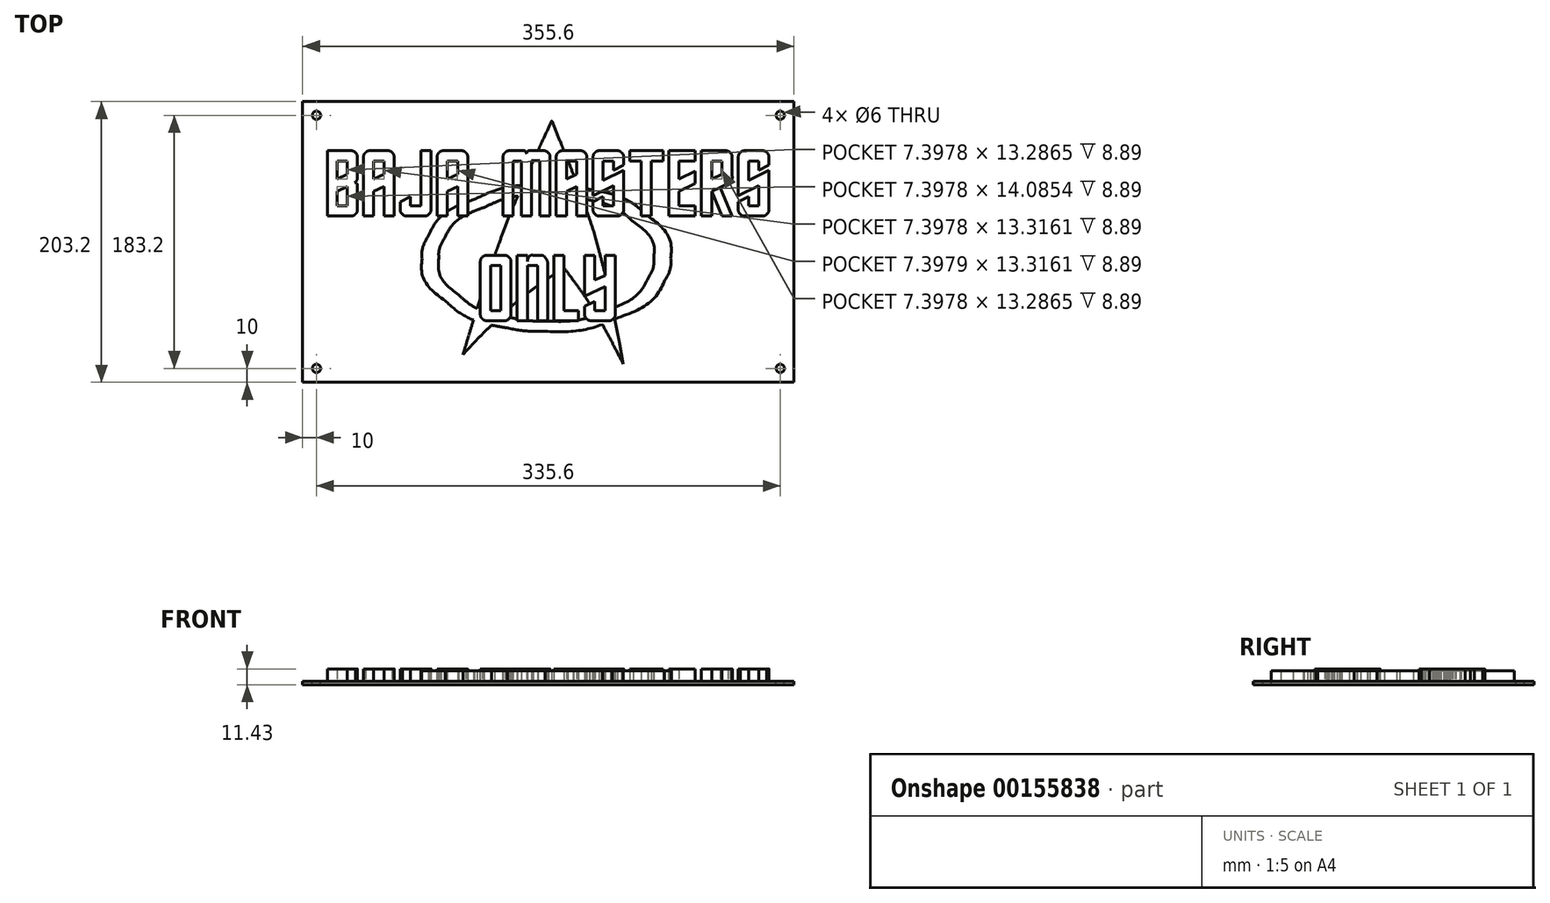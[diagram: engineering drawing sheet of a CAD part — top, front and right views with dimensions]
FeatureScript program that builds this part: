
annotation { "Feature Type Name" : "Feature", "Feature Type Description" : "" }
export const myFeature = defineFeature(function(context is Context, id is Id, definition is map)
    precondition{}
    {
        {
            var Q0;
            Q0=qCreatedBy(makeId("Top.planeOp"),FACE);
            var sketch = newSketch(context, id + "F0", { "sketchPlane" : qUnion([Q0])});
            skLineSegment(sketch, "E0.bottom", {"start": v(177.8, -101.6) * mm, "end": v(-177.8, -101.6) * mm});
            skLineSegment(sketch, "E0.top", {"start": v(177.8, 101.6) * mm, "end": v(-177.8, 101.6) * mm});
            skLineSegment(sketch, "E0.left", {"start": v(177.8, -101.6) * mm, "end": v(177.8, 101.6) * mm});
            skLineSegment(sketch, "E0.right", {"start": v(-177.8, -101.6) * mm, "end": v(-177.8, 101.6) * mm});
            skPoint(sketch, "E0.middle", {"position": v(0, 0) * mm});
            skCircle(sketch, "E1", {"center": v(-167.8, 91.6) * mm, "radius": 3 * mm});
            skCircle(sketch, "E2", {"center": v(-167.8, -91.6) * mm, "radius": 3 * mm});
            skCircle(sketch, "E3", {"center": v(167.8, 91.6) * mm, "radius": 3 * mm});
            skCircle(sketch, "E4", {"center": v(167.8, -91.6) * mm, "radius": 3 * mm});
            skSolve(sketch);
        }
        {
            var Q0;
            Q0=makeQuery(id+"F0.imprint","IMPRINT",FACE,{"disambiguationData":[TD([[makeQuery(id+"F0.imprint","IMPRINT",EDGE,{"derivedFrom":sQuery(id+"F0.wireOp",EDGE,"E0.bottom")}),-1.0]])]});
            var sketch = newSketch(context, id + "F1", { "sketchPlane" : qUnion([Q0])});
            skFitSpline(sketch, "E5", {"points": [v(54.28, -88.47) * mm, v(50.86, -81.9) * mm, v(48.15, -76.64) * mm, v(46.12, -72.72) * mm]});
            skFitSpline(sketch, "E6", {"points": [v(46.12, -72.72) * mm, v(39.8, -60.96) * mm, v(34.36, -51.6) * mm, v(29.8, -44.65) * mm]});
            skFitSpline(sketch, "E7", {"points": [v(29.8, -44.65) * mm, v(26.65, -39.85) * mm, v(22.73, -34.22) * mm, v(18.05, -27.77) * mm]});
            skFitSpline(sketch, "E8", {"points": [v(18.05, -27.77) * mm, v(16.4, -25.5) * mm, v(14.13, -22.46) * mm, v(11.22, -18.67) * mm]});
            skFitSpline(sketch, "E9", {"points": [v(11.22, -18.67) * mm, v(6.54, -21.83) * mm, v(2.88, -24.36) * mm, v(0.22, -26.25) * mm]});
            skFitSpline(sketch, "E10", {"points": [v(0.22, -26.25) * mm, v(-8.5, -32.32) * mm, v(-15.02, -37.13) * mm, v(-19.32, -40.67) * mm]});
            skFitSpline(sketch, "E11", {"points": [v(-19.32, -40.67) * mm, v(-25.13, -45.35) * mm, v(-31.45, -50.97) * mm, v(-38.28, -57.55) * mm]});
            skFitSpline(sketch, "E12", {"points": [v(-38.28, -57.55) * mm, v(-44.23, -63.24) * mm, v(-49.73, -68.74) * mm, v(-54.78, -74.05) * mm]});
            skFitSpline(sketch, "E13", {"points": [v(-54.78, -74.05) * mm, v(-57.19, -76.58) * mm, v(-59.53, -79.1) * mm, v(-61.8, -81.64) * mm]});
            skFitSpline(sketch, "E14", {"points": [v(-61.8, -81.64) * mm, v(-60.41, -77.09) * mm, v(-59.02, -72.47) * mm, v(-57.63, -67.8) * mm]});
            skFitSpline(sketch, "E15", {"points": [v(-57.63, -67.8) * mm, v(-53.08, -53) * mm, v(-49.73, -42.31) * mm, v(-47.58, -35.74) * mm]});
            skFitSpline(sketch, "E16", {"points": [v(-47.58, -35.74) * mm, v(-43.53, -23.47) * mm, v(-39.48, -11.71) * mm, v(-35.44, -0.46) * mm]});
            skFitSpline(sketch, "E17", {"points": [v(-35.44, -0.46) * mm, v(-31.26, 10.92) * mm, v(-26.08, 23.76) * mm, v(-19.88, 38.05) * mm]});
            skFitSpline(sketch, "E18", {"points": [v(-19.88, 38.05) * mm, v(-14.83, 49.8) * mm, v(-9.7, 61.31) * mm, v(-4.52, 72.57) * mm]});
            skFitSpline(sketch, "E19", {"points": [v(-4.52, 72.57) * mm, v(0.03, 82.43) * mm, v(2.37, 87.36) * mm, v(2.5, 87.36) * mm]});
            skFitSpline(sketch, "E20", {"points": [v(2.5, 87.36) * mm, v(2.62, 87.36) * mm, v(4.77, 82.18) * mm, v(8.95, 71.8) * mm]});
            skFitSpline(sketch, "E21", {"points": [v(8.95, 71.8) * mm, v(13.88, 59.67) * mm, v(18.56, 47.53) * mm, v(22.98, 35.39) * mm]});
            skFitSpline(sketch, "E22", {"points": [v(22.98, 35.39) * mm, v(29.05, 18.7) * mm, v(33.6, 4.73) * mm, v(36.64, -6.53) * mm]});
            skFitSpline(sketch, "E23", {"points": [v(36.64, -6.53) * mm, v(39.17, -15.76) * mm, v(41.95, -27.46) * mm, v(44.98, -41.62) * mm]});
            skFitSpline(sketch, "E24", {"points": [v(44.98, -41.62) * mm, v(47.51, -53.25) * mm, v(49.73, -64.06) * mm, v(51.62, -74.05) * mm]});
            skFitSpline(sketch, "E25", {"points": [v(51.62, -74.05) * mm, v(52.5, -78.86) * mm, v(53.4, -83.66) * mm, v(54.28, -88.47) * mm]});
            skFitSpline(sketch, "E26", {"points": [v(84.06, -28.34) * mm, v(77.86, -39.34) * mm, v(66.67, -48.2) * mm, v(50.48, -54.9) * mm]});
            skFitSpline(sketch, "E27", {"points": [v(50.48, -54.9) * mm, v(34.43, -61.47) * mm, v(16.79, -64.76) * mm, v(-2.43, -64.76) * mm]});
            skFitSpline(sketch, "E28", {"points": [v(-2.43, -64.76) * mm, v(-11.92, -64.76) * mm, v(-21.02, -63.94) * mm, v(-29.75, -62.3) * mm]});
            skFitSpline(sketch, "E29", {"points": [v(-29.75, -62.3) * mm, v(-48.34, -58.5) * mm, v(-63.26, -51.99) * mm, v(-74.51, -42.76) * mm]});
            skFitSpline(sketch, "E30", {"points": [v(-74.51, -42.76) * mm, v(-85.76, -33.4) * mm, v(-91.4, -23.16) * mm, v(-91.4, -12.03) * mm]});
            skFitSpline(sketch, "E31", {"points": [v(-91.4, -12.03) * mm, v(-91.4, -6.46) * mm, v(-89.81, -0.96) * mm, v(-86.65, 4.47) * mm]});
            skFitSpline(sketch, "E32", {"points": [v(-86.65, 4.47) * mm, v(-80.45, 15.47) * mm, v(-69.39, 24.26) * mm, v(-53.46, 30.84) * mm]});
            skFitSpline(sketch, "E33", {"points": [v(-53.46, 30.84) * mm, v(-37.52, 37.54) * mm, v(-19.95, 40.9) * mm, v(-0.73, 40.9) * mm]});
            skFitSpline(sketch, "E34", {"points": [v(-0.73, 40.9) * mm, v(9, 40.9) * mm, v(18.24, 40.07) * mm, v(26.96, 38.42) * mm]});
            skFitSpline(sketch, "E35", {"points": [v(26.96, 38.42) * mm, v(45.55, 34.76) * mm, v(60.47, 28.25) * mm, v(71.73, 18.89) * mm]});
            skFitSpline(sketch, "E36", {"points": [v(71.73, 18.89) * mm, v(82.98, 9.53) * mm, v(88.6, -0.77) * mm, v(88.6, -12.03) * mm]});
            skFitSpline(sketch, "E37", {"points": [v(88.6, -12.03) * mm, v(88.6, -17.34) * mm, v(87.1, -22.78) * mm, v(84.06, -28.34) * mm]});
            skFitSpline(sketch, "E38", {"points": [v(72.1, -26.25) * mm, v(74.89, -21.58) * mm, v(76.28, -16.77) * mm, v(76.28, -11.84) * mm]});
            skFitSpline(sketch, "E39", {"points": [v(76.28, -11.84) * mm, v(76.28, -2.23) * mm, v(71.35, 6.56) * mm, v(61.49, 14.53) * mm]});
            skFitSpline(sketch, "E40", {"points": [v(61.49, 14.53) * mm, v(51.75, 22.62) * mm, v(38.85, 28.25) * mm, v(22.8, 31.4) * mm]});
            skFitSpline(sketch, "E41", {"points": [v(22.8, 31.4) * mm, v(14.83, 32.92) * mm, v(6.8, 33.68) * mm, v(-1.3, 33.68) * mm]});
            skFitSpline(sketch, "E42", {"points": [v(-1.3, 33.68) * mm, v(-17.6, 33.68) * mm, v(-32.66, 30.77) * mm, v(-46.44, 24.96) * mm]});
            skFitSpline(sketch, "E43", {"points": [v(-46.44, 24.96) * mm, v(-60.22, 19.27) * mm, v(-69.83, 11.74) * mm, v(-75.27, 2.39) * mm]});
            skFitSpline(sketch, "E44", {"points": [v(-75.27, 2.39) * mm, v(-77.92, -2.42) * mm, v(-79.25, -7.16) * mm, v(-79.25, -11.84) * mm]});
            skFitSpline(sketch, "E45", {"points": [v(-79.25, -11.84) * mm, v(-79.25, -21.45) * mm, v(-74.45, -30.3) * mm, v(-64.84, -38.4) * mm]});
            skFitSpline(sketch, "E46", {"points": [v(-64.84, -38.4) * mm, v(-55.1, -46.36) * mm, v(-42.14, -51.92) * mm, v(-25.95, -55.08) * mm]});
            skFitSpline(sketch, "E47", {"points": [v(-25.95, -55.08) * mm, v(-17.73, -56.6) * mm, v(-9.58, -57.36) * mm, v(-1.49, -57.36) * mm]});
            skFitSpline(sketch, "E48", {"points": [v(-1.49, -57.36) * mm, v(14.95, -57.36) * mm, v(29.94, -54.58) * mm, v(43.47, -49.02) * mm]});
            skFitSpline(sketch, "E49", {"points": [v(43.47, -49.02) * mm, v(57.12, -43.32) * mm, v(66.67, -35.74) * mm, v(72.1, -26.25) * mm]});
            skSolve(sketch);
        }
        {
            var Q0;
            Q0 = qSketchRegion(id + "F1", true);
            var Q1;
            {var subQ8=sQuery(id+"F1.wireOp",EDGE,"E7");Q1=makeQuery(id+"F1.imprint","IMPRINT",FACE,{"disambiguationData":[TD([[makeQuery(id+"F1.imprint","IMPRINT",EDGE,{"derivedFrom":subQ8}),-1.0]])]});}
            extrude(context, id + "F2", {"entities" : qUnion([Q0, Q1]), "depth" : 7.62 * mm});
        }
        {
            var Q0;
            Q0=makeQuery(id+"F0.imprint","IMPRINT",FACE,{"disambiguationData":[TD([[makeQuery(id+"F0.imprint","IMPRINT",EDGE,{"derivedFrom":sQuery(id+"F0.wireOp",EDGE,"E0.bottom")}),-1.0]])]});
            extrude(context, id + "F3", {"entities" : qUnion([Q0]), "operationType" : NewBodyOperationType.ADD, "oppositeDirection" : true, "depth" : 2.54 * mm});
        }
        {
            var Q0;
            Q0=qCreatedBy(makeId("Top.planeOp"),FACE);
            var sketch = newSketch(context, id + "F4", { "sketchPlane" : qUnion([Q0])});
            skLineSegment(sketch, "E50", {"start": v(-145.58, 58.6) * mm, "end": v(-152.98, 58.6) * mm});
            skLineSegment(sketch, "E51", {"start": v(-152.98, 58.6) * mm, "end": v(-152.98, 45.32) * mm});
            skLineSegment(sketch, "E52", {"start": v(-152.98, 45.32) * mm, "end": v(-145.58, 49) * mm});
            skLineSegment(sketch, "E53", {"start": v(-145.58, 49) * mm, "end": v(-145.58, 58.6) * mm});
            skLineSegment(sketch, "E54", {"start": v(-145.58, 40.14) * mm, "end": v(-152.98, 36.45) * mm});
            skLineSegment(sketch, "E55", {"start": v(-152.98, 36.45) * mm, "end": v(-152.98, 26.06) * mm});
            skLineSegment(sketch, "E56", {"start": v(-152.98, 26.06) * mm, "end": v(-145.58, 26.06) * mm});
            skLineSegment(sketch, "E57", {"start": v(-145.58, 26.06) * mm, "end": v(-145.58, 40.14) * mm});
            skFitSpline(sketch, "E58", {"points": [v(-138.19, 26.06) * mm, v(-138.19, 23.1) * mm, v(-138.68, 21.13) * mm, v(-139.67, 20.14) * mm]});
            skFitSpline(sketch, "E59", {"points": [v(-139.67, 20.14) * mm, v(-140.65, 19.15) * mm, v(-142.62, 18.66) * mm, v(-145.58, 18.66) * mm]});
            skLineSegment(sketch, "E60", {"start": v(-138.19, 39.37) * mm, "end": v(-138.19, 26.06) * mm});
            skLineSegment(sketch, "E61", {"start": v(-138.19, 26.06) * mm, "end": v(-138.19, 39.37) * mm});
            skFitSpline(sketch, "E62", {"points": [v(-145.58, 66) * mm, v(-142.62, 66) * mm, v(-140.65, 65.51) * mm, v(-139.67, 64.53) * mm]});
            skFitSpline(sketch, "E63", {"points": [v(-139.67, 64.53) * mm, v(-138.68, 63.54) * mm, v(-138.19, 61.57) * mm, v(-138.19, 58.6) * mm]});
            skLineSegment(sketch, "E64", {"start": v(-145.58, 18.66) * mm, "end": v(-160.38, 18.66) * mm});
            skLineSegment(sketch, "E65", {"start": v(-159.7, 18.66) * mm, "end": v(-159.7, 66) * mm});
            skLineSegment(sketch, "E66", {"start": v(-160.38, 66) * mm, "end": v(-145.58, 66) * mm});
            skLineSegment(sketch, "E67", {"start": v(-145.58, 66) * mm, "end": v(-145.58, 18.66) * mm});
            skFitSpline(sketch, "E68", {"points": [v(-138.19, 48.25) * mm, v(-138.19, 45.79) * mm, v(-138.88, 44.01) * mm, v(-140.26, 42.93) * mm]});
            skFitSpline(sketch, "E69", {"points": [v(-140.26, 42.93) * mm, v(-138.9, 42.51) * mm, v(-138.2, 41.33) * mm, v(-138.19, 39.37) * mm]});
            skLineSegment(sketch, "E70", {"start": v(-138.19, 58.6) * mm, "end": v(-138.19, 48.25) * mm});
            skLineSegment(sketch, "E71", {"start": v(-138.19, 48.25) * mm, "end": v(-138.19, 58.6) * mm});
            skFitSpline(sketch, "E72", {"points": [v(-133.75, 58.6) * mm, v(-133.75, 61.57) * mm, v(-133.25, 63.54) * mm, v(-132.27, 64.53) * mm]});
            skFitSpline(sketch, "E73", {"points": [v(-132.27, 64.53) * mm, v(-131.28, 65.51) * mm, v(-129.3, 66) * mm, v(-126.35, 66) * mm]});
            skLineSegment(sketch, "E74", {"start": v(-126.35, 58.6) * mm, "end": v(-126.35, 45.3) * mm});
            skLineSegment(sketch, "E75", {"start": v(-126.35, 45.3) * mm, "end": v(-118.95, 49) * mm});
            skLineSegment(sketch, "E76", {"start": v(-118.95, 49) * mm, "end": v(-118.95, 58.6) * mm});
            skLineSegment(sketch, "E77", {"start": v(-118.95, 58.6) * mm, "end": v(-126.35, 58.6) * mm});
            skFitSpline(sketch, "E78", {"points": [v(-118.95, 66) * mm, v(-116, 66) * mm, v(-114.02, 65.51) * mm, v(-113.03, 64.53) * mm]});
            skFitSpline(sketch, "E79", {"points": [v(-113.03, 64.53) * mm, v(-112.05, 63.54) * mm, v(-111.55, 61.57) * mm, v(-111.55, 58.6) * mm]});
            skLineSegment(sketch, "E80", {"start": v(-126.35, 66) * mm, "end": v(-118.95, 66) * mm});
            skLineSegment(sketch, "E81", {"start": v(-118.95, 66) * mm, "end": v(-126.35, 66) * mm});
            skLineSegment(sketch, "E82", {"start": v(-111.55, 58.6) * mm, "end": v(-111.55, 18.66) * mm});
            skLineSegment(sketch, "E83", {"start": v(-111.55, 18.66) * mm, "end": v(-118.95, 18.66) * mm});
            skLineSegment(sketch, "E84", {"start": v(-118.95, 18.66) * mm, "end": v(-118.95, 40.11) * mm});
            skLineSegment(sketch, "E85", {"start": v(-118.95, 40.11) * mm, "end": v(-126.35, 36.42) * mm});
            skLineSegment(sketch, "E86", {"start": v(-126.35, 36.42) * mm, "end": v(-126.35, 18.66) * mm});
            skLineSegment(sketch, "E87", {"start": v(-126.35, 18.66) * mm, "end": v(-133.75, 18.66) * mm});
            skLineSegment(sketch, "E88", {"start": v(-133.75, 18.66) * mm, "end": v(-133.75, 58.6) * mm});
            skLineSegment(sketch, "E89", {"start": v(-133.75, 58.6) * mm, "end": v(-111.55, 58.6) * mm});
            skFitSpline(sketch, "E90", {"points": [v(-84.92, 26.09) * mm, v(-84.92, 23.15) * mm, v(-85.42, 21.18) * mm, v(-86.43, 20.17) * mm]});
            skFitSpline(sketch, "E91", {"points": [v(-86.43, 20.17) * mm, v(-87.42, 19.18) * mm, v(-89.38, 18.68) * mm, v(-92.32, 18.66) * mm]});
            skLineSegment(sketch, "E92", {"start": v(-84.92, 66) * mm, "end": v(-84.92, 26.09) * mm});
            skLineSegment(sketch, "E93", {"start": v(-84.92, 26.09) * mm, "end": v(-84.92, 66) * mm});
            skFitSpline(sketch, "E94", {"points": [v(-99.72, 18.7) * mm, v(-102.66, 18.7) * mm, v(-104.63, 19.17) * mm, v(-105.64, 20.14) * mm]});
            skFitSpline(sketch, "E95", {"points": [v(-105.64, 20.14) * mm, v(-106.62, 21.1) * mm, v(-107.12, 23.1) * mm, v(-107.12, 26.12) * mm]});
            skLineSegment(sketch, "E96", {"start": v(-92.32, 18.66) * mm, "end": v(-99.72, 18.7) * mm});
            skLineSegment(sketch, "E97", {"start": v(-99.72, 18.7) * mm, "end": v(-92.32, 18.66) * mm});
            skLineSegment(sketch, "E98", {"start": v(-107.12, 26.12) * mm, "end": v(-107.12, 29.05) * mm});
            skLineSegment(sketch, "E99", {"start": v(-107.12, 29.05) * mm, "end": v(-99.72, 32.75) * mm});
            skLineSegment(sketch, "E100", {"start": v(-99.72, 32.75) * mm, "end": v(-99.72, 26.09) * mm});
            skLineSegment(sketch, "E101", {"start": v(-99.72, 26.09) * mm, "end": v(-92.32, 26.09) * mm});
            skLineSegment(sketch, "E102", {"start": v(-92.32, 26.09) * mm, "end": v(-92.32, 66) * mm});
            skLineSegment(sketch, "E103", {"start": v(-92.32, 66) * mm, "end": v(-84.92, 66) * mm});
            skLineSegment(sketch, "E104", {"start": v(-84.92, 66) * mm, "end": v(-84.92, 66) * mm});
            skFitSpline(sketch, "E105", {"points": [v(-80.48, 58.6) * mm, v(-80.48, 61.57) * mm, v(-79.99, 63.54) * mm, v(-79, 64.53) * mm]});
            skFitSpline(sketch, "E106", {"points": [v(-79, 64.53) * mm, v(-78.02, 65.51) * mm, v(-76.04, 66) * mm, v(-73.09, 66) * mm]});
            skLineSegment(sketch, "E107", {"start": v(-73.09, 58.6) * mm, "end": v(-73.09, 45.3) * mm});
            skLineSegment(sketch, "E108", {"start": v(-73.09, 45.3) * mm, "end": v(-65.69, 49) * mm});
            skLineSegment(sketch, "E109", {"start": v(-65.69, 49) * mm, "end": v(-65.69, 58.6) * mm});
            skLineSegment(sketch, "E110", {"start": v(-65.69, 58.6) * mm, "end": v(-73.09, 58.6) * mm});
            skFitSpline(sketch, "E111", {"points": [v(-65.69, 66) * mm, v(-62.73, 66) * mm, v(-60.76, 65.51) * mm, v(-59.77, 64.53) * mm]});
            skFitSpline(sketch, "E112", {"points": [v(-59.77, 64.53) * mm, v(-58.78, 63.54) * mm, v(-58.29, 61.57) * mm, v(-58.29, 58.6) * mm]});
            skLineSegment(sketch, "E113", {"start": v(-73.09, 66) * mm, "end": v(-65.69, 66) * mm});
            skLineSegment(sketch, "E114", {"start": v(-65.69, 66) * mm, "end": v(-73.09, 66) * mm});
            skFitSpline(sketch, "E115", {"points": [v(-15.77, 63.79) * mm, v(-15.27, 65.27) * mm, v(-14.04, 66) * mm, v(-12.07, 66) * mm]});
            skLineSegment(sketch, "E116", {"start": v(-58.29, 58.6) * mm, "end": v(-58.29, 18.66) * mm});
            skLineSegment(sketch, "E117", {"start": v(-58.29, 18.66) * mm, "end": v(-65.69, 18.66) * mm});
            skLineSegment(sketch, "E118", {"start": v(-65.69, 18.66) * mm, "end": v(-65.69, 40.11) * mm});
            skLineSegment(sketch, "E119", {"start": v(-65.69, 40.11) * mm, "end": v(-73.09, 36.42) * mm});
            skLineSegment(sketch, "E120", {"start": v(-73.09, 36.42) * mm, "end": v(-73.09, 18.66) * mm});
            skLineSegment(sketch, "E121", {"start": v(-73.09, 18.66) * mm, "end": v(-80.48, 18.66) * mm});
            skLineSegment(sketch, "E122", {"start": v(-80.48, 18.66) * mm, "end": v(-80.48, 58.6) * mm});
            skLineSegment(sketch, "E123", {"start": v(-80.48, 58.6) * mm, "end": v(-58.29, 58.6) * mm});
            skFitSpline(sketch, "E124", {"points": [v(-6.15, 66) * mm, v(-3.2, 66) * mm, v(-1.22, 65.51) * mm, v(-0.23, 64.53) * mm]});
            skFitSpline(sketch, "E125", {"points": [v(-0.23, 64.53) * mm, v(0.75, 63.54) * mm, v(1.25, 61.58) * mm, v(1.25, 58.64) * mm]});
            skLineSegment(sketch, "E126", {"start": v(-12.07, 66) * mm, "end": v(-6.15, 66) * mm});
            skLineSegment(sketch, "E127", {"start": v(-6.15, 66) * mm, "end": v(-12.07, 66) * mm});
            skFitSpline(sketch, "E128", {"points": [v(-32.78, 58.6) * mm, v(-32.78, 61.57) * mm, v(-32.29, 63.54) * mm, v(-31.3, 64.53) * mm]});
            skFitSpline(sketch, "E129", {"points": [v(-31.3, 64.53) * mm, v(-30.32, 65.51) * mm, v(-28.34, 66) * mm, v(-25.38, 66) * mm]});
            skLineSegment(sketch, "E130", {"start": v(1.25, 58.64) * mm, "end": v(1.25, 18.66) * mm});
            skLineSegment(sketch, "E131", {"start": v(1.25, 18.66) * mm, "end": v(-6.15, 18.66) * mm});
            skLineSegment(sketch, "E132", {"start": v(-6.15, 18.66) * mm, "end": v(-6.15, 58.64) * mm});
            skLineSegment(sketch, "E133", {"start": v(-6.15, 58.64) * mm, "end": v(-12.07, 58.64) * mm});
            skLineSegment(sketch, "E134", {"start": v(-12.07, 58.64) * mm, "end": v(-12.07, 18.66) * mm});
            skLineSegment(sketch, "E135", {"start": v(-12.07, 18.66) * mm, "end": v(-19.47, 18.66) * mm});
            skLineSegment(sketch, "E136", {"start": v(-19.47, 18.66) * mm, "end": v(-19.47, 58.64) * mm});
            skLineSegment(sketch, "E137", {"start": v(-19.47, 58.64) * mm, "end": v(-25.38, 58.64) * mm});
            skLineSegment(sketch, "E138", {"start": v(-25.38, 58.64) * mm, "end": v(-25.38, 18.66) * mm});
            skLineSegment(sketch, "E139", {"start": v(-25.38, 18.66) * mm, "end": v(-32.78, 18.66) * mm});
            skLineSegment(sketch, "E140", {"start": v(-32.78, 18.66) * mm, "end": v(-32.78, 58.6) * mm});
            skLineSegment(sketch, "E141", {"start": v(-32.78, 58.6) * mm, "end": v(1.25, 58.64) * mm});
            skFitSpline(sketch, "E142", {"points": [v(-19.47, 66) * mm, v(-17.5, 66) * mm, v(-16.26, 65.27) * mm, v(-15.77, 63.79) * mm]});
            skLineSegment(sketch, "E143", {"start": v(-25.38, 66) * mm, "end": v(-19.47, 66) * mm});
            skLineSegment(sketch, "E144", {"start": v(-19.47, 66) * mm, "end": v(-25.38, 66) * mm});
            skFitSpline(sketch, "E145", {"points": [v(5.69, 58.6) * mm, v(5.69, 61.57) * mm, v(6.18, 63.54) * mm, v(7.17, 64.53) * mm]});
            skFitSpline(sketch, "E146", {"points": [v(7.17, 64.53) * mm, v(8.15, 65.51) * mm, v(10.13, 66) * mm, v(13.08, 66) * mm]});
            skLineSegment(sketch, "E147", {"start": v(13.08, 58.6) * mm, "end": v(13.08, 45.3) * mm});
            skLineSegment(sketch, "E148", {"start": v(13.08, 45.3) * mm, "end": v(20.48, 49) * mm});
            skLineSegment(sketch, "E149", {"start": v(20.48, 49) * mm, "end": v(20.48, 58.6) * mm});
            skLineSegment(sketch, "E150", {"start": v(20.48, 58.6) * mm, "end": v(13.08, 58.6) * mm});
            skFitSpline(sketch, "E151", {"points": [v(20.48, 66) * mm, v(23.44, 66) * mm, v(25.41, 65.51) * mm, v(26.4, 64.53) * mm]});
            skFitSpline(sketch, "E152", {"points": [v(26.4, 64.53) * mm, v(27.39, 63.54) * mm, v(27.88, 61.57) * mm, v(27.88, 58.6) * mm]});
            skLineSegment(sketch, "E153", {"start": v(13.08, 66) * mm, "end": v(20.48, 66) * mm});
            skLineSegment(sketch, "E154", {"start": v(20.48, 66) * mm, "end": v(13.08, 66) * mm});
            skFitSpline(sketch, "E155", {"points": [v(32.32, 58.6) * mm, v(32.32, 61.55) * mm, v(32.81, 63.51) * mm, v(33.8, 64.5) * mm]});
            skFitSpline(sketch, "E156", {"points": [v(33.8, 64.5) * mm, v(34.8, 65.5) * mm, v(36.78, 66.02) * mm, v(39.72, 66.04) * mm]});
            skLineSegment(sketch, "E157", {"start": v(27.88, 58.6) * mm, "end": v(27.88, 18.66) * mm});
            skLineSegment(sketch, "E158", {"start": v(27.88, 18.66) * mm, "end": v(20.48, 18.66) * mm});
            skLineSegment(sketch, "E159", {"start": v(20.48, 18.66) * mm, "end": v(20.48, 40.11) * mm});
            skLineSegment(sketch, "E160", {"start": v(20.48, 40.11) * mm, "end": v(13.08, 36.42) * mm});
            skLineSegment(sketch, "E161", {"start": v(13.08, 36.42) * mm, "end": v(13.08, 18.66) * mm});
            skLineSegment(sketch, "E162", {"start": v(13.08, 18.66) * mm, "end": v(5.69, 18.66) * mm});
            skLineSegment(sketch, "E163", {"start": v(5.69, 18.66) * mm, "end": v(5.69, 58.6) * mm});
            skLineSegment(sketch, "E164", {"start": v(5.69, 58.6) * mm, "end": v(27.88, 58.6) * mm});
            skFitSpline(sketch, "E165", {"points": [v(47.11, 66) * mm, v(50.05, 66) * mm, v(52.02, 65.52) * mm, v(53, 64.56) * mm]});
            skFitSpline(sketch, "E166", {"points": [v(53, 64.56) * mm, v(54, 63.6) * mm, v(54.51, 61.6) * mm, v(54.51, 58.58) * mm]});
            skLineSegment(sketch, "E167", {"start": v(39.72, 66.04) * mm, "end": v(47.11, 66) * mm});
            skLineSegment(sketch, "E168", {"start": v(47.11, 66) * mm, "end": v(39.72, 66.04) * mm});
            skFitSpline(sketch, "E169", {"points": [v(54.51, 26.09) * mm, v(54.51, 23.15) * mm, v(54, 21.18) * mm, v(53, 20.17) * mm]});
            skFitSpline(sketch, "E170", {"points": [v(53, 20.17) * mm, v(52.02, 19.18) * mm, v(50.05, 18.68) * mm, v(47.11, 18.66) * mm]});
            skLineSegment(sketch, "E171", {"start": v(54.51, 58.58) * mm, "end": v(54.51, 55.65) * mm});
            skLineSegment(sketch, "E172", {"start": v(54.51, 55.65) * mm, "end": v(47.11, 51.95) * mm});
            skLineSegment(sketch, "E173", {"start": v(47.11, 51.95) * mm, "end": v(47.11, 58.6) * mm});
            skLineSegment(sketch, "E174", {"start": v(47.11, 58.6) * mm, "end": v(39.72, 58.6) * mm});
            skLineSegment(sketch, "E175", {"start": v(39.72, 58.6) * mm, "end": v(39.72, 44.55) * mm});
            skLineSegment(sketch, "E176", {"start": v(39.72, 44.55) * mm, "end": v(54.51, 51.95) * mm});
            skLineSegment(sketch, "E177", {"start": v(54.51, 51.95) * mm, "end": v(54.51, 26.09) * mm});
            skFitSpline(sketch, "E178", {"points": [v(39.72, 18.7) * mm, v(36.78, 18.7) * mm, v(34.8, 19.17) * mm, v(33.8, 20.14) * mm]});
            skFitSpline(sketch, "E179", {"points": [v(33.8, 20.14) * mm, v(32.81, 21.1) * mm, v(32.32, 23.1) * mm, v(32.32, 26.12) * mm]});
            skLineSegment(sketch, "E180", {"start": v(47.11, 18.66) * mm, "end": v(39.72, 18.7) * mm});
            skLineSegment(sketch, "E181", {"start": v(39.72, 18.7) * mm, "end": v(47.11, 18.66) * mm});
            skLineSegment(sketch, "E182", {"start": v(32.32, 26.12) * mm, "end": v(32.32, 29.05) * mm});
            skLineSegment(sketch, "E183", {"start": v(32.32, 29.05) * mm, "end": v(39.72, 32.75) * mm});
            skLineSegment(sketch, "E184", {"start": v(39.72, 32.75) * mm, "end": v(39.72, 26.09) * mm});
            skLineSegment(sketch, "E185", {"start": v(39.72, 26.09) * mm, "end": v(47.11, 26.09) * mm});
            skLineSegment(sketch, "E186", {"start": v(47.11, 26.09) * mm, "end": v(47.11, 40.82) * mm});
            skLineSegment(sketch, "E187", {"start": v(47.11, 40.82) * mm, "end": v(32.32, 33.46) * mm});
            skLineSegment(sketch, "E188", {"start": v(32.32, 33.46) * mm, "end": v(32.32, 58.6) * mm});
            skLineSegment(sketch, "E189", {"start": v(67.09, 18.66) * mm, "end": v(67.09, 58.6) * mm});
            skLineSegment(sketch, "E190", {"start": v(67.09, 58.6) * mm, "end": v(58.95, 58.58) * mm});
            skLineSegment(sketch, "E191", {"start": v(58.95, 58.58) * mm, "end": v(58.95, 66) * mm});
            skLineSegment(sketch, "E192", {"start": v(58.95, 66) * mm, "end": v(82.92, 66) * mm});
            skLineSegment(sketch, "E193", {"start": v(82.92, 66) * mm, "end": v(82.92, 58.58) * mm});
            skLineSegment(sketch, "E194", {"start": v(82.92, 58.58) * mm, "end": v(74.49, 58.58) * mm});
            skLineSegment(sketch, "E195", {"start": v(74.49, 58.58) * mm, "end": v(74.49, 18.66) * mm});
            skLineSegment(sketch, "E196", {"start": v(74.49, 18.66) * mm, "end": v(67.09, 18.66) * mm});
            skLineSegment(sketch, "E197", {"start": v(67.09, 18.66) * mm, "end": v(67.09, 18.66) * mm});
            skLineSegment(sketch, "E198", {"start": v(87.12, 66) * mm, "end": v(106.36, 66) * mm});
            skLineSegment(sketch, "E199", {"start": v(106.36, 66) * mm, "end": v(106.36, 58.6) * mm});
            skLineSegment(sketch, "E200", {"start": v(106.36, 58.6) * mm, "end": v(94.52, 58.6) * mm});
            skLineSegment(sketch, "E201", {"start": v(94.52, 58.6) * mm, "end": v(94.52, 45.32) * mm});
            skLineSegment(sketch, "E202", {"start": v(94.52, 45.32) * mm, "end": v(106.36, 51.21) * mm});
            skLineSegment(sketch, "E203", {"start": v(106.36, 51.21) * mm, "end": v(106.36, 42.36) * mm});
            skLineSegment(sketch, "E204", {"start": v(106.36, 42.36) * mm, "end": v(94.52, 36.45) * mm});
            skLineSegment(sketch, "E205", {"start": v(94.52, 36.45) * mm, "end": v(94.52, 26.06) * mm});
            skLineSegment(sketch, "E206", {"start": v(94.52, 26.06) * mm, "end": v(106.36, 26.06) * mm});
            skLineSegment(sketch, "E207", {"start": v(106.36, 26.06) * mm, "end": v(106.33, 18.66) * mm});
            skLineSegment(sketch, "E208", {"start": v(106.33, 18.66) * mm, "end": v(87.12, 18.66) * mm});
            skLineSegment(sketch, "E209", {"start": v(87.12, 18.66) * mm, "end": v(87.12, 66) * mm});
            skLineSegment(sketch, "E210", {"start": v(87.12, 66) * mm, "end": v(87.12, 66) * mm});
            skLineSegment(sketch, "E211", {"start": v(125.6, 58.6) * mm, "end": v(118.2, 58.6) * mm});
            skLineSegment(sketch, "E212", {"start": v(118.2, 58.6) * mm, "end": v(118.2, 45.32) * mm});
            skLineSegment(sketch, "E213", {"start": v(118.2, 45.32) * mm, "end": v(125.6, 49) * mm});
            skLineSegment(sketch, "E214", {"start": v(125.6, 49) * mm, "end": v(125.6, 58.6) * mm});
            skFitSpline(sketch, "E215", {"points": [v(125.6, 66) * mm, v(128.55, 66) * mm, v(130.52, 65.51) * mm, v(131.5, 64.53) * mm]});
            skFitSpline(sketch, "E216", {"points": [v(131.5, 64.53) * mm, v(132.5, 63.54) * mm, v(132.99, 61.57) * mm, v(132.99, 58.6) * mm]});
            skLineSegment(sketch, "E217", {"start": v(118.25, 36.47) * mm, "end": v(118.2, 36.45) * mm});
            skLineSegment(sketch, "E218", {"start": v(118.2, 36.45) * mm, "end": v(118.2, 18.66) * mm});
            skLineSegment(sketch, "E219", {"start": v(118.2, 18.66) * mm, "end": v(110.8, 18.66) * mm});
            skLineSegment(sketch, "E220", {"start": v(110.8, 18.66) * mm, "end": v(110.8, 66) * mm});
            skLineSegment(sketch, "E221", {"start": v(110.8, 66) * mm, "end": v(125.6, 66) * mm});
            skFitSpline(sketch, "E222", {"points": [v(132.99, 48.25) * mm, v(132.99, 45.3) * mm, v(132, 43.33) * mm, v(130.03, 42.36) * mm]});
            skLineSegment(sketch, "E223", {"start": v(132.99, 58.6) * mm, "end": v(132.99, 48.25) * mm});
            skLineSegment(sketch, "E224", {"start": v(132.99, 48.25) * mm, "end": v(132.99, 58.6) * mm});
            skFitSpline(sketch, "E225", {"points": [v(137.43, 58.6) * mm, v(137.43, 61.55) * mm, v(137.92, 63.51) * mm, v(138.9, 64.5) * mm]});
            skFitSpline(sketch, "E226", {"points": [v(138.9, 64.5) * mm, v(139.91, 65.5) * mm, v(141.89, 66.02) * mm, v(144.82, 66.04) * mm]});
            skLineSegment(sketch, "E227", {"start": v(130.03, 42.36) * mm, "end": v(124.38, 39.55) * mm});
            skLineSegment(sketch, "E228", {"start": v(124.38, 39.55) * mm, "end": v(132.99, 18.66) * mm});
            skLineSegment(sketch, "E229", {"start": v(132.99, 18.66) * mm, "end": v(125.6, 18.66) * mm});
            skLineSegment(sketch, "E230", {"start": v(125.6, 18.66) * mm, "end": v(118.25, 36.47) * mm});
            skLineSegment(sketch, "E231", {"start": v(118.25, 36.47) * mm, "end": v(118.25, 36.47) * mm});
            skLineSegment(sketch, "E232", {"start": v(118.25, 36.47) * mm, "end": v(130.03, 42.36) * mm});
            skFitSpline(sketch, "E233", {"points": [v(152.22, 66) * mm, v(155.16, 66) * mm, v(157.13, 65.52) * mm, v(158.11, 64.56) * mm]});
            skFitSpline(sketch, "E234", {"points": [v(158.11, 64.56) * mm, v(159.12, 63.6) * mm, v(159.62, 61.6) * mm, v(159.62, 58.58) * mm]});
            skLineSegment(sketch, "E235", {"start": v(144.82, 66.04) * mm, "end": v(152.22, 66) * mm});
            skLineSegment(sketch, "E236", {"start": v(152.22, 66) * mm, "end": v(144.82, 66.04) * mm});
            skFitSpline(sketch, "E237", {"points": [v(159.62, 26.09) * mm, v(159.62, 23.15) * mm, v(159.12, 21.18) * mm, v(158.11, 20.17) * mm]});
            skFitSpline(sketch, "E238", {"points": [v(158.11, 20.17) * mm, v(157.13, 19.18) * mm, v(155.16, 18.68) * mm, v(152.22, 18.66) * mm]});
            skLineSegment(sketch, "E239", {"start": v(159.62, 58.58) * mm, "end": v(159.62, 55.65) * mm});
            skLineSegment(sketch, "E240", {"start": v(159.62, 55.65) * mm, "end": v(152.22, 51.95) * mm});
            skLineSegment(sketch, "E241", {"start": v(152.22, 51.95) * mm, "end": v(152.22, 58.6) * mm});
            skLineSegment(sketch, "E242", {"start": v(152.22, 58.6) * mm, "end": v(144.82, 58.6) * mm});
            skLineSegment(sketch, "E243", {"start": v(144.82, 58.6) * mm, "end": v(144.82, 44.55) * mm});
            skLineSegment(sketch, "E244", {"start": v(144.82, 44.55) * mm, "end": v(159.62, 51.95) * mm});
            skLineSegment(sketch, "E245", {"start": v(159.62, 51.95) * mm, "end": v(159.62, 26.09) * mm});
            skLineSegment(sketch, "E246", {"start": v(160.3, 26.09) * mm, "end": v(160.3, 58.58) * mm});
            skFitSpline(sketch, "E247", {"points": [v(144.82, 18.7) * mm, v(141.89, 18.7) * mm, v(139.91, 19.17) * mm, v(138.9, 20.14) * mm]});
            skFitSpline(sketch, "E248", {"points": [v(138.9, 20.14) * mm, v(137.92, 21.1) * mm, v(137.43, 23.1) * mm, v(137.43, 26.12) * mm]});
            skLineSegment(sketch, "E249", {"start": v(152.22, 18.66) * mm, "end": v(144.82, 18.7) * mm});
            skLineSegment(sketch, "E250", {"start": v(144.82, 18.7) * mm, "end": v(152.22, 18.66) * mm});
            skFitSpline(sketch, "E251", {"points": [v(-34.44, -9.75) * mm, v(-31.5, -9.75) * mm, v(-29.54, -10.23) * mm, v(-28.55, -11.2) * mm]});
            skFitSpline(sketch, "E252", {"points": [v(-28.55, -11.2) * mm, v(-27.54, -12.16) * mm, v(-27.04, -14.16) * mm, v(-27.04, -17.17) * mm]});
            skLineSegment(sketch, "E253", {"start": v(137.43, 26.12) * mm, "end": v(137.43, 29.05) * mm});
            skLineSegment(sketch, "E254", {"start": v(137.43, 29.05) * mm, "end": v(144.82, 32.75) * mm});
            skLineSegment(sketch, "E255", {"start": v(144.82, 32.75) * mm, "end": v(144.82, 26.09) * mm});
            skLineSegment(sketch, "E256", {"start": v(144.82, 26.09) * mm, "end": v(152.22, 26.09) * mm});
            skLineSegment(sketch, "E257", {"start": v(152.22, 26.09) * mm, "end": v(152.22, 40.82) * mm});
            skLineSegment(sketch, "E258", {"start": v(152.22, 40.82) * mm, "end": v(137.43, 33.46) * mm});
            skLineSegment(sketch, "E259", {"start": v(137.43, 33.46) * mm, "end": v(137.43, 58.6) * mm});
            skFitSpline(sketch, "E260", {"points": [v(-27.04, -49.7) * mm, v(-27.04, -52.65) * mm, v(-27.53, -54.63) * mm, v(-28.52, -55.61) * mm]});
            skFitSpline(sketch, "E261", {"points": [v(-28.52, -55.61) * mm, v(-29.5, -56.6) * mm, v(-31.48, -57.1) * mm, v(-34.44, -57.1) * mm]});
            skLineSegment(sketch, "E262", {"start": v(-27.04, -17.17) * mm, "end": v(-27.04, -49.7) * mm});
            skLineSegment(sketch, "E263", {"start": v(-27.04, -49.7) * mm, "end": v(-27.04, -17.17) * mm});
            skFitSpline(sketch, "E264", {"points": [v(-41.84, -57.1) * mm, v(-44.8, -57.1) * mm, v(-46.77, -56.6) * mm, v(-47.76, -55.61) * mm]});
            skFitSpline(sketch, "E265", {"points": [v(-47.76, -55.61) * mm, v(-48.74, -54.63) * mm, v(-49.23, -52.66) * mm, v(-49.23, -49.72) * mm]});
            skLineSegment(sketch, "E266", {"start": v(-34.44, -57.1) * mm, "end": v(-41.84, -57.1) * mm});
            skLineSegment(sketch, "E267", {"start": v(-41.84, -57.1) * mm, "end": v(-34.44, -57.1) * mm});
            skFitSpline(sketch, "E268", {"points": [v(-49.23, -17.14) * mm, v(-49.23, -14.2) * mm, v(-48.74, -12.24) * mm, v(-47.76, -11.26) * mm]});
            skFitSpline(sketch, "E269", {"points": [v(-47.76, -11.26) * mm, v(-46.75, -10.25) * mm, v(-44.78, -9.74) * mm, v(-41.84, -9.72) * mm]});
            skLineSegment(sketch, "E270", {"start": v(-49.23, -49.72) * mm, "end": v(-49.23, -17.14) * mm});
            skLineSegment(sketch, "E271", {"start": v(-49.23, -17.14) * mm, "end": v(-49.23, -49.72) * mm});
            skLineSegment(sketch, "E272", {"start": v(-41.84, -9.72) * mm, "end": v(-34.44, -9.75) * mm});
            skLineSegment(sketch, "E273", {"start": v(-34.44, -9.75) * mm, "end": v(-34.44, -9.75) * mm});
            skLineSegment(sketch, "E274", {"start": v(-34.44, -9.75) * mm, "end": v(-41.84, -9.72) * mm});
            skLineSegment(sketch, "E275", {"start": v(-34.44, -49.72) * mm, "end": v(-34.44, -17.14) * mm});
            skLineSegment(sketch, "E276", {"start": v(-34.44, -17.14) * mm, "end": v(-41.84, -17.14) * mm});
            skLineSegment(sketch, "E277", {"start": v(-41.84, -17.14) * mm, "end": v(-41.84, -49.72) * mm});
            skLineSegment(sketch, "E278", {"start": v(-41.84, -49.72) * mm, "end": v(-34.44, -49.72) * mm});
            skFitSpline(sketch, "E279", {"points": [v(-15.2, -14.19) * mm, v(-14.22, -11.23) * mm, v(-12.74, -9.75) * mm, v(-10.77, -9.75) * mm]});
            skLineSegment(sketch, "E280", {"start": v(-22.6, -9.75) * mm, "end": v(-15.2, -9.75) * mm});
            skLineSegment(sketch, "E281", {"start": v(-15.2, -9.75) * mm, "end": v(-15.2, -14.19) * mm});
            skFitSpline(sketch, "E282", {"points": [v(-7.8, -9.75) * mm, v(-4.85, -9.75) * mm, v(-2.87, -10.49) * mm, v(-1.89, -11.97) * mm]});
            skFitSpline(sketch, "E283", {"points": [v(-1.89, -11.97) * mm, v(-0.9, -13.45) * mm, v(-0.4, -15.17) * mm, v(-0.4, -17.14) * mm]});
            skLineSegment(sketch, "E284", {"start": v(-10.77, -9.75) * mm, "end": v(-7.8, -9.75) * mm});
            skLineSegment(sketch, "E285", {"start": v(-7.8, -9.75) * mm, "end": v(-10.77, -9.75) * mm});
            skLineSegment(sketch, "E286", {"start": v(-0.4, -17.14) * mm, "end": v(-0.4, -57.1) * mm});
            skLineSegment(sketch, "E287", {"start": v(-0.4, -57.1) * mm, "end": v(-7.8, -57.1) * mm});
            skLineSegment(sketch, "E288", {"start": v(-7.8, -57.1) * mm, "end": v(-7.8, -17.14) * mm});
            skLineSegment(sketch, "E289", {"start": v(-7.8, -17.14) * mm, "end": v(-15.2, -17.14) * mm});
            skLineSegment(sketch, "E290", {"start": v(-15.2, -17.14) * mm, "end": v(-15.2, -57.1) * mm});
            skLineSegment(sketch, "E291", {"start": v(-15.2, -57.1) * mm, "end": v(-22.6, -57.1) * mm});
            skLineSegment(sketch, "E292", {"start": v(-22.6, -57.1) * mm, "end": v(-22.6, -9.75) * mm});
            skLineSegment(sketch, "E293", {"start": v(4.03, -9.72) * mm, "end": v(11.43, -9.72) * mm});
            skLineSegment(sketch, "E294", {"start": v(11.43, -9.72) * mm, "end": v(11.43, -49.7) * mm});
            skLineSegment(sketch, "E295", {"start": v(11.43, -49.7) * mm, "end": v(21.75, -49.7) * mm});
            skLineSegment(sketch, "E296", {"start": v(21.75, -49.7) * mm, "end": v(21.75, -57.1) * mm});
            skLineSegment(sketch, "E297", {"start": v(21.75, -57.1) * mm, "end": v(4.03, -57.1) * mm});
            skLineSegment(sketch, "E298", {"start": v(4.03, -57.1) * mm, "end": v(4.03, -9.72) * mm});
            skFitSpline(sketch, "E299", {"points": [v(48.48, -49.67) * mm, v(48.48, -52.6) * mm, v(47.97, -54.58) * mm, v(46.97, -55.58) * mm]});
            skFitSpline(sketch, "E300", {"points": [v(46.97, -55.58) * mm, v(45.98, -56.57) * mm, v(44.02, -57.07) * mm, v(41.08, -57.1) * mm]});
            skLineSegment(sketch, "E301", {"start": v(41.08, -9.75) * mm, "end": v(48.48, -9.75) * mm});
            skLineSegment(sketch, "E302", {"start": v(48.48, -9.75) * mm, "end": v(48.48, -49.67) * mm});
            skFitSpline(sketch, "E303", {"points": [v(33.68, -57.06) * mm, v(30.74, -57.06) * mm, v(28.77, -56.58) * mm, v(27.76, -55.61) * mm]});
            skFitSpline(sketch, "E304", {"points": [v(27.76, -55.61) * mm, v(26.78, -54.65) * mm, v(26.28, -52.65) * mm, v(26.28, -49.64) * mm]});
            skLineSegment(sketch, "E305", {"start": v(41.08, -57.1) * mm, "end": v(33.68, -57.06) * mm});
            skLineSegment(sketch, "E306", {"start": v(33.68, -57.06) * mm, "end": v(41.08, -57.1) * mm});
            skLineSegment(sketch, "E307", {"start": v(26.28, -49.64) * mm, "end": v(26.28, -46.7) * mm});
            skLineSegment(sketch, "E308", {"start": v(26.28, -46.7) * mm, "end": v(33.68, -43) * mm});
            skLineSegment(sketch, "E309", {"start": v(33.68, -43) * mm, "end": v(33.68, -49.67) * mm});
            skLineSegment(sketch, "E310", {"start": v(33.68, -49.67) * mm, "end": v(41.08, -49.67) * mm});
            skLineSegment(sketch, "E311", {"start": v(41.08, -49.67) * mm, "end": v(41.08, -32.44) * mm});
            skLineSegment(sketch, "E312", {"start": v(41.08, -32.44) * mm, "end": v(26.28, -39.34) * mm});
            skLineSegment(sketch, "E313", {"start": v(26.28, -39.34) * mm, "end": v(26.28, -9.75) * mm});
            skLineSegment(sketch, "E314", {"start": v(26.28, -9.75) * mm, "end": v(33.68, -9.75) * mm});
            skLineSegment(sketch, "E315", {"start": v(33.68, -9.75) * mm, "end": v(33.68, -27.47) * mm});
            skLineSegment(sketch, "E316", {"start": v(33.68, -27.47) * mm, "end": v(41.08, -24.54) * mm});
            skLineSegment(sketch, "E317", {"start": v(41.08, -24.54) * mm, "end": v(41.08, -9.75) * mm});
            skLineSegment(sketch, "E318", {"start": v(41.08, -9.75) * mm, "end": v(41.08, -9.75) * mm});
            skLineSegment(sketch, "E319", {"start": v(-92.32, 26.09) * mm, "end": v(-92.32, 18.66) * mm});
            skLineSegment(sketch, "E320", {"start": v(-92.32, 26.09) * mm, "end": v(-84.92, 26.09) * mm});
            skLineSegment(sketch, "E321", {"start": v(-92.32, 66) * mm, "end": v(-84.92, 26.09) * mm});
            skLineSegment(sketch, "E322", {"start": v(-84.92, 30.08) * mm, "end": v(-84.92, 26.09) * mm});
            skLineSegment(sketch, "E323", {"start": v(-84.92, 26.09) * mm, "end": v(-92.32, 66) * mm});
            skLineSegment(sketch, "E324", {"start": v(-92.32, 26.09) * mm, "end": v(-84.92, 66) * mm});
            skLineSegment(sketch, "E325", {"start": v(67.09, 58.6) * mm, "end": v(74.49, 58.58) * mm});
            skLineSegment(sketch, "E326", {"start": v(67.09, 58.6) * mm, "end": v(74.49, 18.66) * mm});
            skLineSegment(sketch, "E327", {"start": v(67.09, 18.66) * mm, "end": v(74.49, 18.66) * mm});
            skLineSegment(sketch, "E328", {"start": v(94.52, 45.32) * mm, "end": v(94.52, 36.45) * mm});
            skLineSegment(sketch, "E329", {"start": v(94.52, 58.6) * mm, "end": v(87.12, 66) * mm});
            skLineSegment(sketch, "E330", {"start": v(94.52, 26.06) * mm, "end": v(87.12, 18.66) * mm});
            skLineSegment(sketch, "E331", {"start": v(94.52, 45.32) * mm, "end": v(87.12, 42.33) * mm});
            skLineSegment(sketch, "E332", {"start": v(87.12, 42.33) * mm, "end": v(94.52, 58.6) * mm});
            skLineSegment(sketch, "E333", {"start": v(87.12, 66) * mm, "end": v(87.12, 42.33) * mm});
            skLineSegment(sketch, "E334", {"start": v(124.38, 39.55) * mm, "end": v(125.6, 18.66) * mm});
            skLineSegment(sketch, "E335", {"start": v(118.25, 36.47) * mm, "end": v(125.6, 18.66) * mm});
            skLineSegment(sketch, "E336", {"start": v(118.25, 36.47) * mm, "end": v(124.38, 39.55) * mm});
            skSolve(sketch);
        }
        {
            var Q0;
            Q0 = qSketchRegion(id + "F4", true);
            extrude(context, id + "F5", {"entities" : qUnion([Q0]), "operationType" : NewBodyOperationType.ADD, "depth" : 8.9 * mm});
        }
    });
